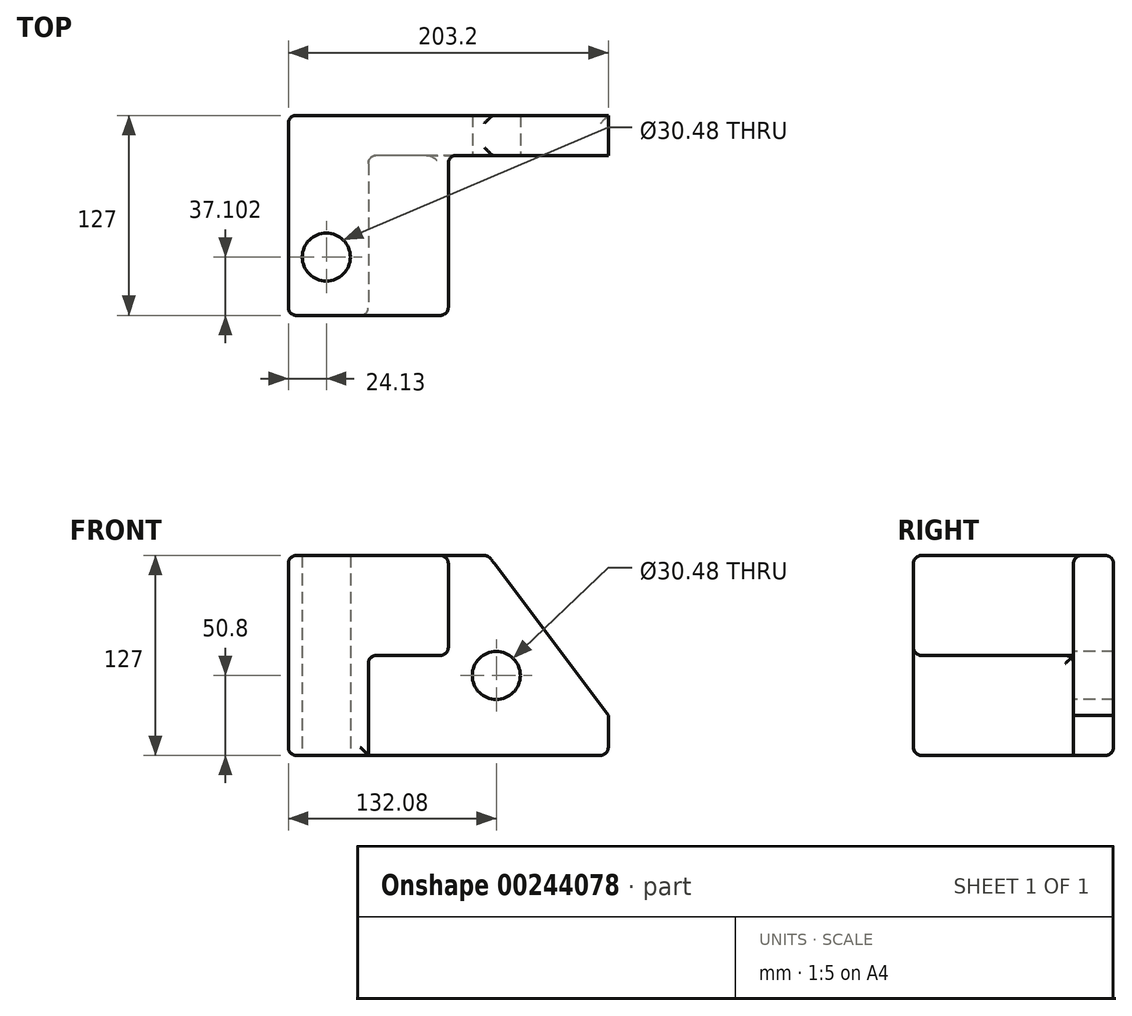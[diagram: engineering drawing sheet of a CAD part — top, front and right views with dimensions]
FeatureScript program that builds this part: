
annotation { "Feature Type Name" : "Feature", "Feature Type Description" : "" }
export const myFeature = defineFeature(function(context is Context, id is Id, definition is map)
    precondition{}
    {
        {
            var Q0;
            Q0=qCreatedBy(makeId("Front.planeOp"),FACE);
            var sketch = newSketch(context, id + "F0", { "sketchPlane" : qUnion([Q0])});
            skLineSegment(sketch, "E0.bottom", {"start": v(101.6, 63.5) * mm, "end": v(-101.6, 63.5) * mm});
            skLineSegment(sketch, "E0.top", {"start": v(101.6, -63.5) * mm, "end": v(-101.6, -63.5) * mm});
            skLineSegment(sketch, "E0.left", {"start": v(101.6, 63.5) * mm, "end": v(101.6, -63.5) * mm});
            skLineSegment(sketch, "E0.right", {"start": v(-101.6, 63.5) * mm, "end": v(-101.6, -63.5) * mm});
            skPoint(sketch, "E0.middle", {"position": v(0, 0) * mm});
            skSolve(sketch);
        }
        {
            var Q0;
            Q0 = qSketchRegion(id + "F0", true);
            extrude(context, id + "F1", {"entities" : qUnion([Q0]), "depth" : 127 * mm});
        }
        {
            var Q0;
            Q0=makeQuery(id+"F1.opExtrude","CAP_FACE",FACE,{"disambiguationData":[OSD([sQuery(id+"F0.wireOp",EDGE,"E0.bottom"),sQuery(id+"F0.wireOp",EDGE,"E0.top"),sQuery(id+"F0.wireOp",EDGE,"E0.left"),sQuery(id+"F0.wireOp",EDGE,"E0.right")])],"isStart":false});
            var sketch = newSketch(context, id + "F2", { "sketchPlane" : qUnion([Q0])});
            skLineSegment(sketch, "E1", {"start": v(-101.6, 63.5) * mm, "end": v(0, 63.5) * mm});
            skLineSegment(sketch, "E2", {"start": v(0, 63.5) * mm, "end": v(0, 0) * mm});
            skLineSegment(sketch, "E3", {"start": v(0, 0) * mm, "end": v(-50.8, 0) * mm});
            skLineSegment(sketch, "E4", {"start": v(-50.8, 0) * mm, "end": v(-50.8, -63.5) * mm});
            skLineSegment(sketch, "E5", {"start": v(-50.8, -63.5) * mm, "end": v(-101.6, -63.5) * mm});
            skLineSegment(sketch, "E6", {"start": v(-101.6, -63.5) * mm, "end": v(-101.6, 63.5) * mm});
            skSolve(sketch);
        }
        {
            var Q0;
            {var subQ2=sQuery(id+"F2.wireOp",EDGE,"E2");Q0=makeQuery(id+"F2.imprint","IMPRINT",FACE,{"disambiguationData":[TD([[makeQuery(id+"F2.imprint","IMPRINT",EDGE,{"derivedFrom":subQ2}),1.0]])]});}
            extrude(context, id + "F3", {"entities" : qUnion([Q0]), "operationType" : NewBodyOperationType.REMOVE, "oppositeDirection" : true, "depth" : 101.6 * mm});
        }
        {
            var Q0;
            Q0=makeQuery(id+"F1.opExtrude","SWEPT_EDGE",EDGE,{"disambiguationData":[OSD([sQuery(id+"F0.wireOp",EDGE,"E0.bottom"),sQuery(id+"F0.wireOp",EDGE,"E0.left")])]});
            chamfer(context, id + "F4", {"entities" : qUnion([Q0]), "chamferType" : ChamferType.TWO_OFFSETS, "width1" : 76.2 * mm, "oppositeDirection" : false, "width2" : 101.6 * mm, "tangentPropagation" : true});
        }
        {
            var Q0;
            Q0=makeQuery(id+"F1.opExtrude","CAP_EDGE",EDGE,{"disambiguationData":[OSD([sQuery(id+"F0.wireOp",EDGE,"E0.right")])],"isStart":true});
            var Q1;
            Q1=makeQuery(id+"F3.boolean.opBoolean","COPY",EDGE,{"derivedFrom":makeQuery(id+"F3.opExtrude","SWEPT_EDGE",EDGE,{"disambiguationData":[OSD([sQuery(id+"F2.wireOp",EDGE,"E3"),sQuery(id+"F2.wireOp",EDGE,"E4")])]})});
            var Q2;
            Q2=makeQuery(id+"F3.boolean.opBoolean","COPY",EDGE,{"derivedFrom":makeQuery(id+"F3.opExtrude","SWEPT_EDGE",EDGE,{"disambiguationData":[OSD([sQuery(id+"F0.wireOp",EDGE,"E0.top"),sQuery(id+"F2.wireOp",EDGE,"E4"),sQuery(id+"F2.wireOp",EDGE,"E5")])]})});
            var Q3;
            Q3=makeQuery(id+"F3.boolean.opBoolean","COPY",EDGE,{"derivedFrom":makeQuery(id+"F3.opExtrude","CAP_EDGE",EDGE,{"disambiguationData":[OSD([sQuery(id+"F2.wireOp",EDGE,"E2")])],"isStart":true})});
            var Q4;
            Q4=makeQuery(id+"F3.boolean.opBoolean","COPY",EDGE,{"derivedFrom":makeQuery(id+"F3.opExtrude","CAP_EDGE",EDGE,{"disambiguationData":[OSD([sQuery(id+"F2.wireOp",EDGE,"E3")])],"isStart":true})});
            var Q5;
            Q5=makeQuery(id+"F3.boolean.opBoolean","COPY",EDGE,{"derivedFrom":makeQuery(id+"F3.opExtrude","CAP_EDGE",EDGE,{"disambiguationData":[OSD([sQuery(id+"F2.wireOp",EDGE,"E4")])],"isStart":true})});
            var Q6;
            Q6=makeQuery(id+"F3.boolean.opBoolean","COPY",EDGE,{"derivedFrom":makeQuery(id+"F3.opExtrude","CAP_EDGE",EDGE,{"disambiguationData":[OSD([sQuery(id+"F2.wireOp",EDGE,"E4")])],"isStart":false})});
            var Q7;
            Q7=makeQuery(id+"F1.opExtrude","CAP_FACE",FACE,{"disambiguationData":[OSD([sQuery(id+"F0.wireOp",EDGE,"E0.bottom"),sQuery(id+"F0.wireOp",EDGE,"E0.top"),sQuery(id+"F0.wireOp",EDGE,"E0.left"),sQuery(id+"F0.wireOp",EDGE,"E0.right")])],"isStart":false});
            var Q8;
            Q8=makeQuery(id+"F1.opExtrude","SWEPT_FACE",FACE,{"disambiguationData":[OSD([sQuery(id+"F0.wireOp",EDGE,"E0.bottom")])]});
            var Q9;
            Q9=makeQuery(id+"F1.opExtrude","SWEPT_EDGE",EDGE,{"disambiguationData":[OSD([sQuery(id+"F0.wireOp",EDGE,"E0.top"),sQuery(id+"F0.wireOp",EDGE,"E0.left")])]});
            var Q10;
            Q10=makeQuery(id+"F3.boolean.opBoolean","COPY",EDGE,{"derivedFrom":makeQuery(id+"F3.opExtrude","SWEPT_EDGE",EDGE,{"disambiguationData":[OSD([sQuery(id+"F2.wireOp",EDGE,"E2"),sQuery(id+"F2.wireOp",EDGE,"E3")])]})});
            var Q11;
            Q11=makeQuery(id+"F3.boolean.opBoolean","COPY",EDGE,{"derivedFrom":makeQuery(id+"F3.opExtrude","CAP_EDGE",EDGE,{"disambiguationData":[OSD([sQuery(id+"F2.wireOp",EDGE,"E2")])],"isStart":false})});
            var Q12;
            Q12=makeQuery(id+"F1.opExtrude","CAP_EDGE",EDGE,{"disambiguationData":[OSD([sQuery(id+"F0.wireOp",EDGE,"E0.top")])],"isStart":true});
            fillet(context, id + "F5", {"entities" : qUnion([Q0, Q1, Q2, Q3, Q4, Q5, Q6, Q7, Q8, Q9, Q10, Q11, Q12]), "radius" : 5.08 * mm, "tangentPropagation" : true, "allowEdgeOverflow" : false});
        }
        {
            var Q0;
            Q0=makeQuery(id+"F3.boolean.opBoolean","COPY",FACE,{"derivedFrom":makeQuery(id+"F3.opExtrude","CAP_FACE",FACE,{"disambiguationData":[OSD([sQuery(id+"F0.wireOp",EDGE,"E0.bottom"),sQuery(id+"F0.wireOp",EDGE,"E0.top"),sQuery(id+"F0.wireOp",EDGE,"E0.left"),sQuery(id+"F2.wireOp",EDGE,"E2"),sQuery(id+"F2.wireOp",EDGE,"E3"),sQuery(id+"F2.wireOp",EDGE,"E4")])],"isStart":false})});
            var sketch = newSketch(context, id + "F6", { "sketchPlane" : qUnion([Q0])});
            skCircle(sketch, "E7", {"center": v(30.48, -12.7) * mm, "radius": 15.24 * mm});
            skSolve(sketch);
        }
        {
            var Q0;
            Q0=makeQuery(id+"F6.imprint","IMPRINT",FACE,{"disambiguationData":[TD([[makeQuery(id+"F6.imprint","IMPRINT",EDGE,{"derivedFrom":sQuery(id+"F6.wireOp",EDGE,"E7")}),1.0]])]});
            var Q1;
            Q1=makeQuery(id+"F1.opExtrude","CAP_FACE",FACE,{"disambiguationData":[OSD([sQuery(id+"F0.wireOp",EDGE,"E0.bottom"),sQuery(id+"F0.wireOp",EDGE,"E0.top"),sQuery(id+"F0.wireOp",EDGE,"E0.left"),sQuery(id+"F0.wireOp",EDGE,"E0.right")])],"isStart":true});
            extrude(context, id + "F7", {"entities" : qUnion([Q0]), "operationType" : NewBodyOperationType.REMOVE, "endBound" : BoundingType.UP_TO_SURFACE, "oppositeDirection" : true, "endBoundEntityFace" : qUnion([Q1]), "depth" : 25.4 * mm});
        }
        {
            var Q0;
            Q0=makeQuery(id+"F1.opExtrude","SWEPT_EDGE",EDGE,{"disambiguationData":[OSD([sQuery(id+"F0.wireOp",EDGE,"E0.top"),sQuery(id+"F0.wireOp",EDGE,"E0.right")])]});
            fillet(context, id + "F8", {"entities" : qUnion([Q0]), "radius" : 5.08 * mm, "tangentPropagation" : true, "allowEdgeOverflow" : false});
        }
        {
            var Q0;
            Q0=makeQuery(id+"F1.opExtrude","SWEPT_FACE",FACE,{"disambiguationData":[OSD([sQuery(id+"F0.wireOp",EDGE,"E0.top")])]});
            var sketch = newSketch(context, id + "F9", { "sketchPlane" : qUnion([Q0])});
            skCircle(sketch, "E8", {"center": v(-77.47, 89.9) * mm, "radius": 15.24 * mm});
            skSolve(sketch);
        }
        {
            var Q0;
            Q0 = qSketchRegion(id + "F9", true);
            var Q1;
            Q1=makeQuery(id+"F1.opExtrude","SWEPT_FACE",FACE,{"disambiguationData":[OSD([sQuery(id+"F0.wireOp",EDGE,"E0.bottom")])]});
            extrude(context, id + "F10", {"entities" : qUnion([Q0]), "operationType" : NewBodyOperationType.REMOVE, "endBound" : BoundingType.UP_TO_SURFACE, "oppositeDirection" : true, "endBoundEntityFace" : qUnion([Q1]), "depth" : 25.4 * mm});
        }
    });
